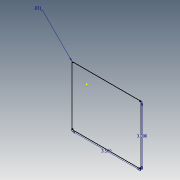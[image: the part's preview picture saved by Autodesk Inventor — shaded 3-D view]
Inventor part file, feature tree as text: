
AUTODESK INVENTOR PART (.ipt)
format: ipt  version: 2013 SP2 (Build 170200200, 200)  size: 99,840 bytes
history: native  units: in
note: dims shown in document units (in); Inventor stores cm internally (conversion verified against a paired STEP export)
features: sketch x1
ambient origin geometry x8: Origin, YZ Plane, XZ Plane, XY Plane, X Axis, Y Axis, Z Axis, Center Point
feature tree (1):
  sketch  "Sketch1"  dims[d0=3.5in d1=3.0in d2=0.0312in]
